# Revit family: Electronics_Conferencing-Bars_Biamp_Parle_Speaker_SBC-2__
name_source: partatom
category: Communication Devices
units: mm (PartAtom-declared; Revit-internal decimal feet)

## family parameters
Cut with Voids When Loaded = No
Host = Face
Maintain Annotation Orientation = No
OmniClass Number = 23.85.10.11.14
OmniClass Title = Audio Equipment
Part Type = Normal
Room Calculation Point = No
Round Connector Dimension = Use Diameter
Shared = No

## types (1)
- SBC 2
    Apparent Load = 60 VA
    CEC Support = Yes
    Codec = 24-bit PCM stereo
    Compliance = CE Marked (Europe) RoHS Directive (Europe)
    Connector = RCA
    Connector Description = 100-240VAC 50/60Hz
    Default Elevation = 48 "
    Depth = 3 "
    Description = Parlé™ SBC 2 Conferencing Speaker Bar
    Frequency Response = ± 3 dB
    Height = 5.1 "
    Housing Material = Biamp - Plastic - Black
    Input Impedance = < 20kΩ
    Manufacturer = Biamp
    Max Input Level = 1 Vrms
    Max Power Consumption = 60 W
    Maximum SPL = 106 dBA
    Model = Parlé SBC 2
    Number of Inputs = 1 (stereo)
    Number of Poles = 1
    Power Factor = 1
    Product Documentation Link = https://downloads.biamp.com
    Product Page URL = https://www.biamp.com
    Product data url = https://www.bimobject.com
    RS-232 = 19200/8-N-1
    Rated Power = 4 x 20 Wrms
    Sample Rate = 44.1/48 kHz
    Supported Version = 1.4
    THD+N = < 0.1 %
    URL = https://www.biamp.com
    USB Codec = 24-bit PCM stereo
    USB Connector = USB 2.0 Type-B
    USB Sample Rate = 44.1/48 kHz
    Voltage = 120 V
    Wake on Signal = Yes
    Weight = 9.90 lbf
    Width = 40.1 "

## geometry (parser evidence)
native form markers: Sweep x2
no freeform markers — native parametric forms only
